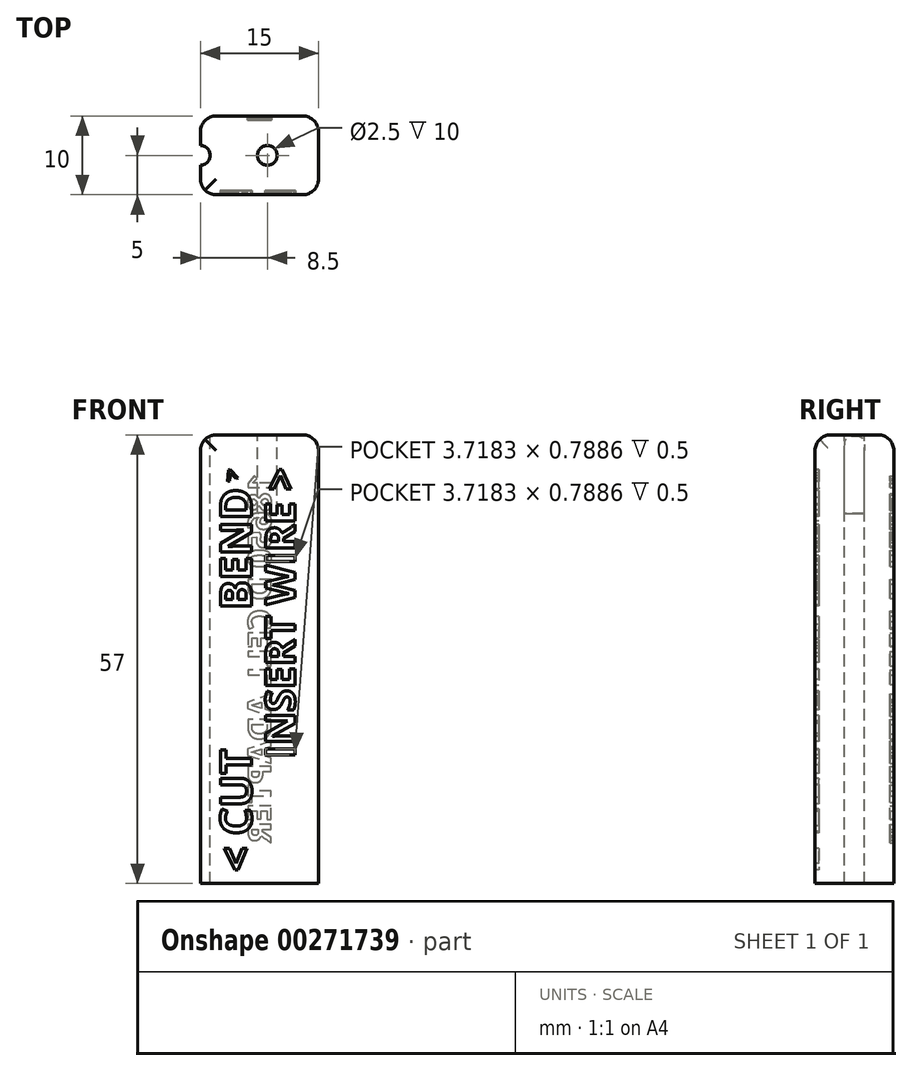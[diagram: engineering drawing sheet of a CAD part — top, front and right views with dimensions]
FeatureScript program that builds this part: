
annotation { "Feature Type Name" : "Feature", "Feature Type Description" : "" }
export const myFeature = defineFeature(function(context is Context, id is Id, definition is map)
    precondition{}
    {
        {
            var Q0;
            Q0=qCreatedBy(makeId("Top.planeOp"),FACE);
            var sketch = newSketch(context, id + "F0", { "sketchPlane" : qUnion([Q0])});
            skLineSegment(sketch, "E0.bottom", {"start": v(-7.5, 5) * mm, "end": v(7.5, 5) * mm});
            skLineSegment(sketch, "E0.top", {"start": v(-7.5, -5) * mm, "end": v(7.5, -5) * mm});
            skLineSegment(sketch, "E0.left", {"start": v(-7.5, 5) * mm, "end": v(-7.5, -5) * mm});
            skLineSegment(sketch, "E0.right", {"start": v(7.5, 5) * mm, "end": v(7.5, -5) * mm});
            skSolve(sketch);
        }
        {
            var Q0;
            Q0 = qSketchRegion(id + "F0", true);
            var Q1;
            Q1=makeQuery(id+"F0.imprint","IMPRINT",FACE,{"disambiguationData":[TD([[makeQuery(id+"F0.imprint","IMPRINT",EDGE,{"derivedFrom":sQuery(id+"F0.wireOp",EDGE,"E0.bottom")}),-1.0]])]});
            extrude(context, id + "F1", {"entities" : qUnion([Q0, Q1]), "depth" : 57 * mm});
        }
        {
            var Q0;
            Q0=makeQuery(id+"F1.opExtrude","CAP_FACE",FACE,{"disambiguationData":[OSD([sQuery(id+"F0.wireOp",EDGE,"E0.bottom"),sQuery(id+"F0.wireOp",EDGE,"E0.top"),sQuery(id+"F0.wireOp",EDGE,"E0.left"),sQuery(id+"F0.wireOp",EDGE,"E0.right")])],"isStart":false});
            var sketch = newSketch(context, id + "F2", { "sketchPlane" : qUnion([Q0])});
            skCircle(sketch, "E1", {"center": v(1, 0) * mm, "radius": 1.25 * mm});
            skSolve(sketch);
        }
        {
            var Q0;
            Q0 = qSketchRegion(id + "F2", true);
            extrude(context, id + "F3", {"entities" : qUnion([Q0]), "operationType" : NewBodyOperationType.REMOVE, "oppositeDirection" : true, "depth" : 10 * mm});
        }
        {
            var Q0;
            Q0=makeQuery(id+"F1.opExtrude","CAP_FACE",FACE,{"disambiguationData":[OSD([sQuery(id+"F0.wireOp",EDGE,"E0.bottom"),sQuery(id+"F0.wireOp",EDGE,"E0.top"),sQuery(id+"F0.wireOp",EDGE,"E0.left"),sQuery(id+"F0.wireOp",EDGE,"E0.right")])],"isStart":false});
            var sketch = newSketch(context, id + "F4", { "sketchPlane" : qUnion([Q0])});
            skArc(sketch, "E2", {"start": v(-7.5, -1.25) * mm, "mid": v(-6.25, 0) * mm, "end": v(-7.5, 1.25) * mm});
            skLineSegment(sketch, "E3", {"start": v(-7.5, -1.25) * mm, "end": v(-7.5, 1.25) * mm});
            skSolve(sketch);
        }
        {
            var Q0;
            Q0 = qSketchRegion(id + "F4", true);
            extrude(context, id + "F5", {"entities" : qUnion([Q0]), "operationType" : NewBodyOperationType.REMOVE, "oppositeDirection" : true, "depth" : 57 * mm});
        }
        {
            var Q0;
            {var subQ0=sQuery(id+"F0.wireOp",EDGE,"E0.bottom");var subQ1=sQuery(id+"F0.wireOp",EDGE,"E0.left");Q0=makeQuery(id+"F5.boolean.opBoolean","SPLIT",EDGE,{"disambiguationData":[TD([makeQuery(id+"F1.opExtrude","SWEPT_FACE",FACE,{"disambiguationData":[OSD([subQ0])]})])],"derivedFrom":makeQuery(id+"F1.opExtrude","CAP_EDGE",EDGE,{"disambiguationData":[OSD([subQ1])],"isStart":false})});}
            var Q1;
            Q1=makeQuery(id+"F1.opExtrude","CAP_EDGE",EDGE,{"disambiguationData":[OSD([sQuery(id+"F0.wireOp",EDGE,"E0.top")])],"isStart":false});
            var Q2;
            Q2=makeQuery(id+"F1.opExtrude","CAP_EDGE",EDGE,{"disambiguationData":[OSD([sQuery(id+"F0.wireOp",EDGE,"E0.right")])],"isStart":false});
            var Q3;
            Q3=makeQuery(id+"F1.opExtrude","CAP_EDGE",EDGE,{"disambiguationData":[OSD([sQuery(id+"F0.wireOp",EDGE,"E0.bottom")])],"isStart":false});
            var Q4;
            Q4=makeQuery(id+"F1.opExtrude","SWEPT_EDGE",EDGE,{"disambiguationData":[OSD([sQuery(id+"F0.wireOp",EDGE,"E0.bottom"),sQuery(id+"F0.wireOp",EDGE,"E0.right")])]});
            var Q5;
            Q5=makeQuery(id+"F1.opExtrude","SWEPT_EDGE",EDGE,{"disambiguationData":[OSD([sQuery(id+"F0.wireOp",EDGE,"E0.top"),sQuery(id+"F0.wireOp",EDGE,"E0.right")])]});
            var Q6;
            Q6=makeQuery(id+"F1.opExtrude","SWEPT_EDGE",EDGE,{"disambiguationData":[OSD([sQuery(id+"F0.wireOp",EDGE,"E0.bottom"),sQuery(id+"F0.wireOp",EDGE,"E0.left")])]});
            var Q7;
            Q7=makeQuery(id+"F1.opExtrude","SWEPT_EDGE",EDGE,{"disambiguationData":[OSD([sQuery(id+"F0.wireOp",EDGE,"E0.top"),sQuery(id+"F0.wireOp",EDGE,"E0.left")])]});
            fillet(context, id + "F6", {"entities" : qUnion([Q0, Q1, Q2, Q3, Q4, Q5, Q6, Q7]), "radius" : 2 * mm, "tangentPropagation" : true, "allowEdgeOverflow" : false});
        }
        {
            var Q0;
            Q0=makeQuery(id+"F1.opExtrude","SWEPT_FACE",FACE,{"disambiguationData":[OSD([sQuery(id+"F0.wireOp",EDGE,"E0.top")])]});
            var sketch = newSketch(context, id + "F7", { "sketchPlane" : qUnion([Q0])});
            skText(sketch, "E4", { "text": "INSERT WIRE >", "fontName": "OpenSans-Bold.ttf"});
            skLineSegment(sketch, "E5", {"start": v(0.75, 15.85) * mm, "end": v(0.75, 15.85) * mm});
            skText(sketch, "E6", { "text": "BEND", "fontName": "OpenSans-Bold.ttf"});
            skText(sketch, "E7", { "text": ">", "fontName": "OpenSans-Bold.ttf"});
            skText(sketch, "E8", { "text": "< CUT", "fontName": "OpenSans-Bold.ttf"});
            const initialGuessF7  = {"E4": [0.0045, 0.01585, 0, 1, 0.00375], "E6": [-0.001, 0.03477, 0, 1, 0.004], "E7": [-0.0024, 0.05152, -0.34202, 0.9397, 0.002], "E8": [-0.001, 0.0015, 0, 1, 0.004]};
            skSetInitialGuess(sketch, initialGuessF7);
            skSolve(sketch);
        }
        {
            var Q0;
            Q0 = qSketchRegion(id + "F7", true);
            extrude(context, id + "F8", {"entities" : qUnion([Q0]), "operationType" : NewBodyOperationType.REMOVE, "oppositeDirection" : true, "depth" : .5 * mm});
        }
        {
            var Q0;
            Q0=makeQuery(id+"F1.opExtrude","SWEPT_FACE",FACE,{"disambiguationData":[OSD([sQuery(id+"F0.wireOp",EDGE,"E0.bottom")])]});
            var sketch = newSketch(context, id + "F9", { "sketchPlane" : qUnion([Q0])});
            skText(sketch, "E9", { "text": "18650 D CELL ADAPTER", "fontName": "OpenSans-Bold.ttf"});
            const initialGuessF9  = {"E9": [-0.0015, 0.052, 0, -1, 0.003]};
            skSetInitialGuess(sketch, initialGuessF9);
            skSolve(sketch);
        }
        {
            var Q0;
            Q0 = qSketchRegion(id + "F9", true);
            extrude(context, id + "F10", {"entities" : qUnion([Q0]), "operationType" : NewBodyOperationType.REMOVE, "oppositeDirection" : true, "depth" : .5 * mm});
        }
    });
